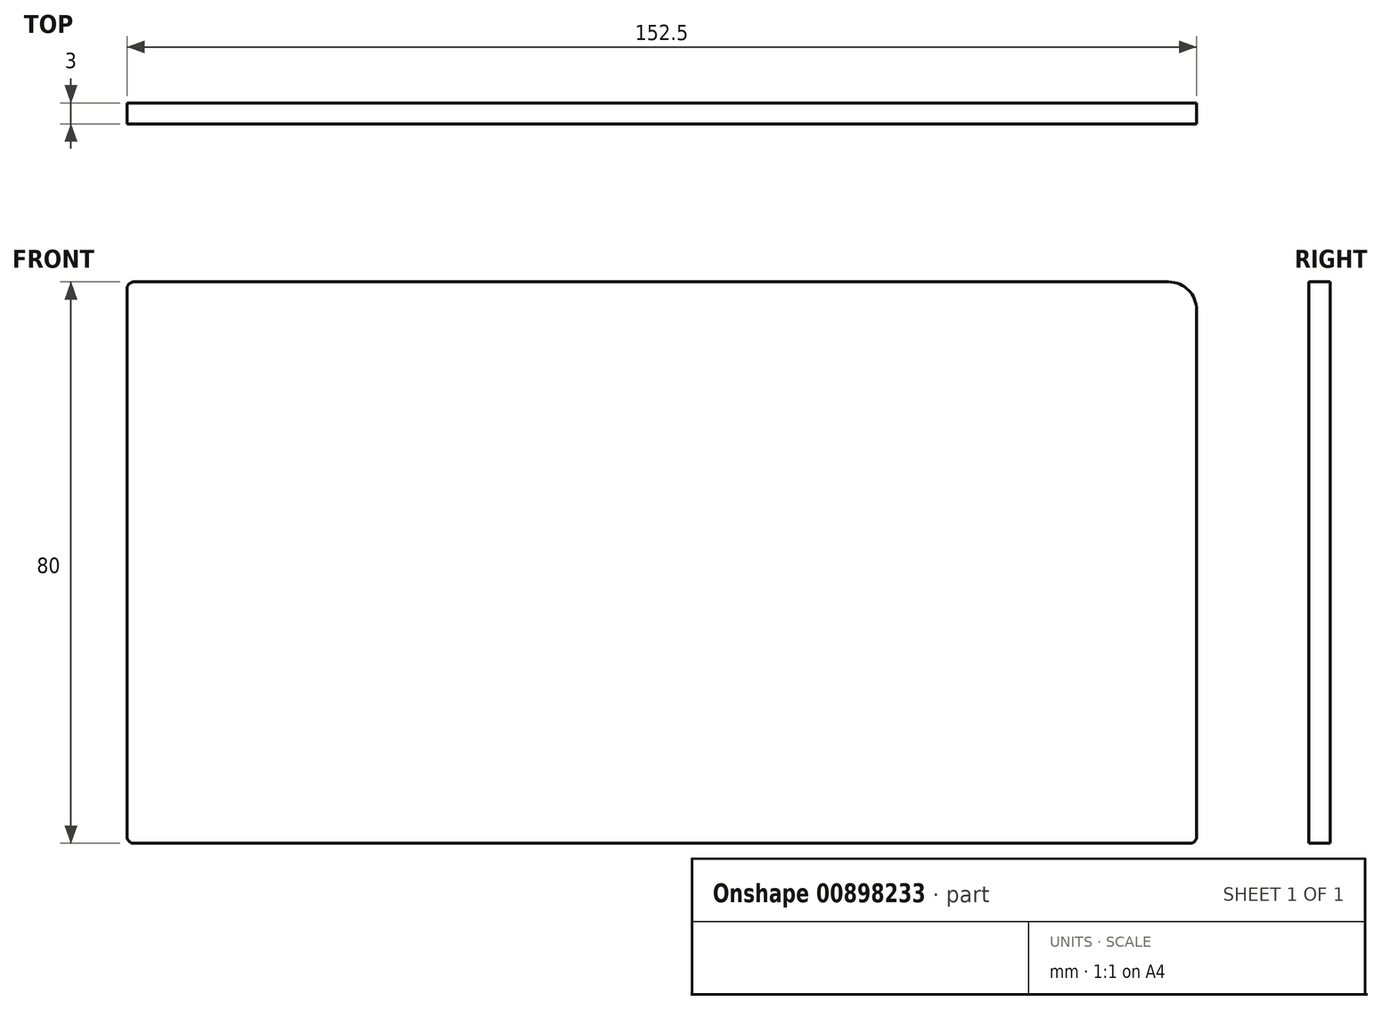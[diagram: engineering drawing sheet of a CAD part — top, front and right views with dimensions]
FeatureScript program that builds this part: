
annotation { "Feature Type Name" : "Feature", "Feature Type Description" : "" }
export const myFeature = defineFeature(function(context is Context, id is Id, definition is map)
    precondition{}
    {
        {
            var Q0;
            Q0=qCreatedBy(makeId("Front.planeOp"),FACE);
            var sketch = newSketch(context, id + "F0", { "sketchPlane" : qUnion([Q0])});
            skLineSegment(sketch, "E0.bottom", {"start": v(0, 0) * mm, "end": v(152.5, 0) * mm});
            skLineSegment(sketch, "E0.top", {"start": v(0, 80) * mm, "end": v(148.5, 80) * mm});
            skLineSegment(sketch, "E0.left", {"start": v(0, 0) * mm, "end": v(0, 80) * mm});
            skLineSegment(sketch, "E0.right", {"start": v(152.5, 0) * mm, "end": v(152.5, 76) * mm});
            skPoint(sketch, "E1.visualSharp", {"position": v(152.5, 80) * mm});
            skArc(sketch, "E1.filletArc", {"start": v(152.5, 76) * mm, "mid": v(151.33, 78.83) * mm, "end": v(148.5, 80) * mm});
            skSolve(sketch);
        }
        {
            var Q0;
            Q0=qSketchRegion(id+"F0",true);
            extrude(context, id + "F1", {"entities" : qUnion([Q0]), "endBound" : BoundingType.SYMMETRIC, "depth" : 3 * mm});
        }
        {
            var Q0;
            Q0=makeQuery(id+"F1.opExtrude","SWEPT_EDGE",EDGE,{"disambiguationData":[OSD([sQuery(id+"F0.wireOp",EDGE,"E0.bottom"),sQuery(id+"F0.wireOp",EDGE,"E0.right")])]});
            var Q1;
            Q1=makeQuery(id+"F1.opExtrude","SWEPT_EDGE",EDGE,{"disambiguationData":[OSD([sQuery(id+"F0.wireOp",EDGE,"E0.top"),sQuery(id+"F0.wireOp",EDGE,"E0.left")])]});
            var Q2;
            Q2=makeQuery(id+"F1.opExtrude","SWEPT_EDGE",EDGE,{"disambiguationData":[OSD([sQuery(id+"F0.wireOp",EDGE,"E0.bottom"),sQuery(id+"F0.wireOp",EDGE,"E0.left")])]});
            fillet(context, id + "F2", {"entities" : qUnion([Q0, Q1, Q2]), "radius" : 1 * mm, "tangentPropagation" : true, "allowEdgeOverflow" : false});
        }
    });
